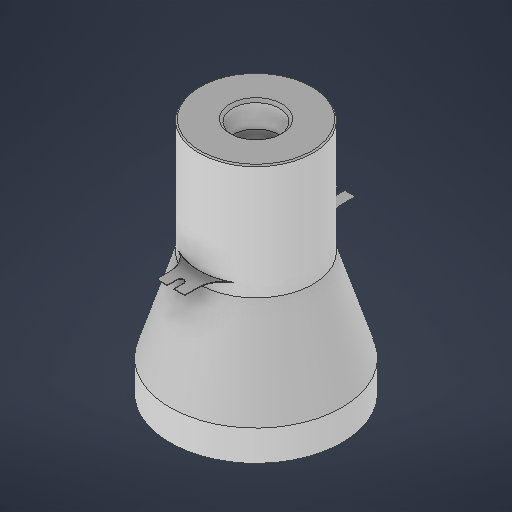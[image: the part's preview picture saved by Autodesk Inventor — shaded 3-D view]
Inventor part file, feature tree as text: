
AUTODESK INVENTOR PART (.ipt)
format: ipt  version: 2025 (Build 290162000, 162)  size: 332,288 bytes
history: native  units: mm
features: sketch x10, plane x5, loft x5, other x3, hole x2, chamfer x2, extrude x1
ambient origin geometry x8: Origin, YZ Plane, XZ Plane, XY Plane, X Axis, Y Axis, Z Axis, Center Point
bodies: Solid1 (feature_tree)
feature tree (28):
  sketch  "Sketch1"  dims[d0=44.8mm d1=40.5mm]
  plane  "Work Plane1"
  sketch  "Sketch2"  dims[d2=-81.5mm d3=-12.0mm d4=67.6mm]
  plane  "Work Plane3"
  sketch  "Sketch3"  dims[d5=0.0mm d6=90.0deg d7=0.0mm d8=90.0deg]
  sketch  "Sketch4"  dims[d13=0.0mm d14=90.0deg d15=0.0mm d16=90.0deg]
  loft  "Loft1"
  loft  "Loft3"
  extrude  "Extrusion1"  TaperAngle=0.0deg  [1 undecoded]
  plane  "Work Plane4"
  sketch  "Sketch6"  dims[d19=10.0mm d20=2.6mm]
  plane  "Work Plane5"
  loft  "Loft4"
  loft  "Loft5"
  loft  "Loft6"
  hole  "Hole1"  [1 undecoded]
  chamfer  "Chamfer1"  Distance=0.2mm
  chamfer  "Chamfer2"  Angle=90.0deg  [1 undecoded]
  hole  "Hole2"  [1 undecoded]
  plane  "Work Plane2"
  other  "Edges2"
  sketch  "Sketch5"  dims[d17=11.0mm d18=67.2mm]
  sketch  "Sketch7"  dims[d21=5.2mm d22=1.3mm d23=0.2mm d24=0.0mm]
  other  "Edges3"
  sketch  "Sketch8"  dims[d25=-4.7mm]
  other  "Edges4"
  sketch  "Sketch9"  dims[d26=-93.5mm d27=0.0mm d28=90.0deg]
  sketch  "Sketch10"  dims[d29=0.0mm d30=90.0deg d31=0.0mm d32=90.0deg d33=0.0mm d34=90.0deg d35=0.0mm d36=90.0deg d37=0.0mm d38=90.0deg d39=18.4mm d40=6.0mm d41=4.0mm d42=2.0mm d43=90.0deg d44=10.0mm d45=0.0mm d46=1.0mm d47=2.0mm d48=45.0deg d49=0.5mm d50=2.0mm d51=45.0deg d52=13.5mm d53=6.0mm d54=4.0mm d55=2.0mm d56=90.0deg d57=10.0mm d58=0.0mm]
note: 4 required parameter values undecoded (feature->parameter linkage not recoverable at this tier; creation-order binding heuristic only, values carry confidence <= 0.55)
